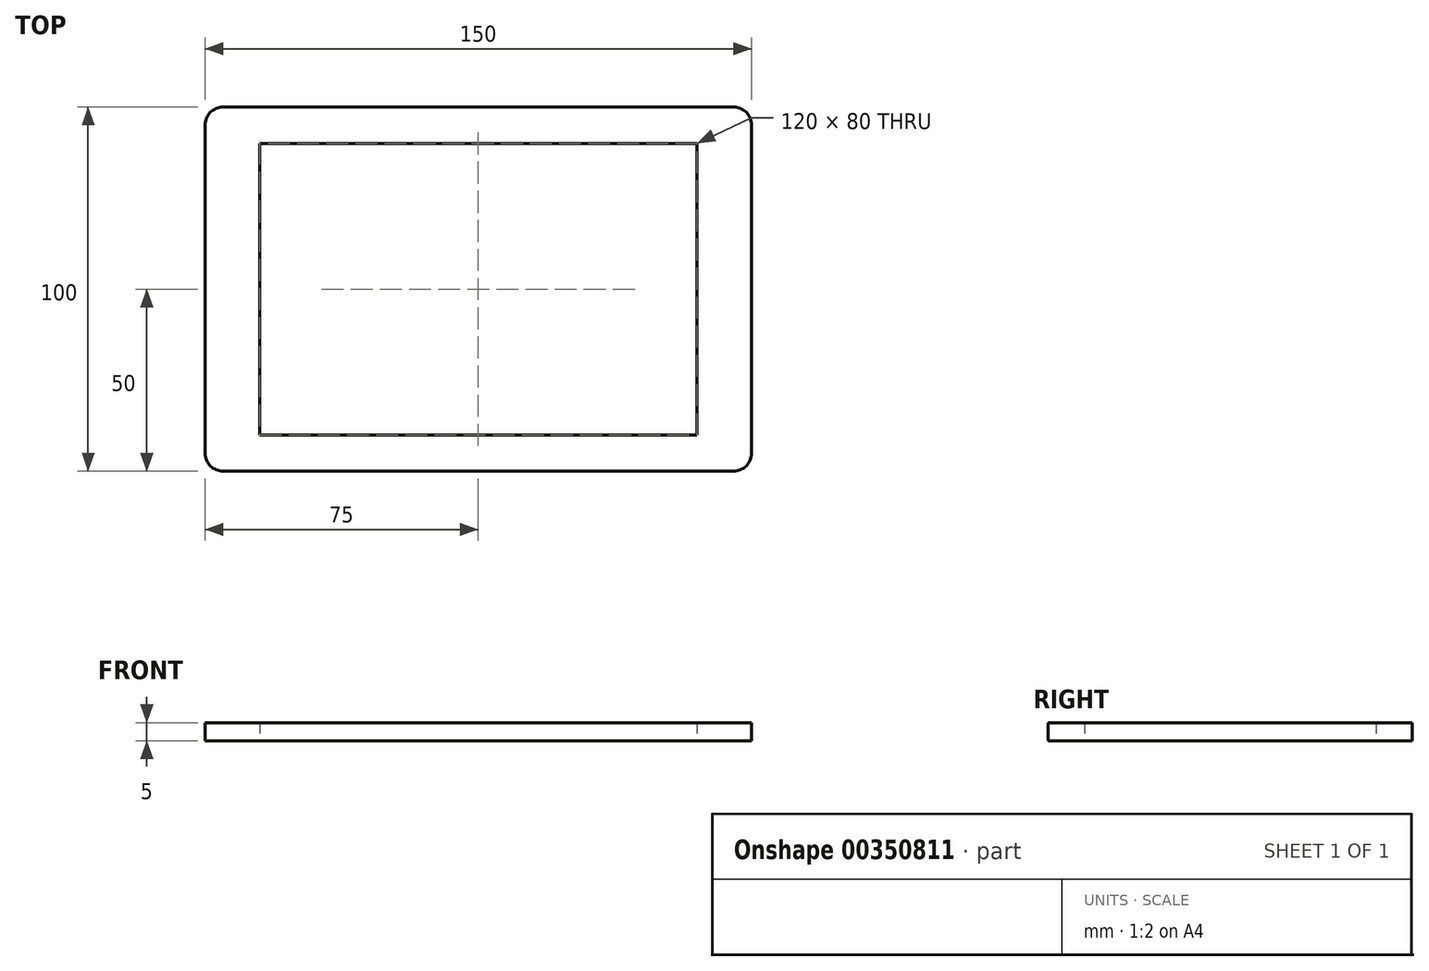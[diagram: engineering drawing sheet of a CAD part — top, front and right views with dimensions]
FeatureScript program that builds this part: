
annotation { "Feature Type Name" : "Feature", "Feature Type Description" : "" }
export const myFeature = defineFeature(function(context is Context, id is Id, definition is map)
    precondition{}
    {
        {
            var Q0;
            Q0=qCreatedBy(makeId("Top.planeOp"),FACE);
            var sketch = newSketch(context, id + "F0", { "sketchPlane" : qUnion([Q0])});
            skLineSegment(sketch, "E0.bottom", {"start": v(70, 50) * mm, "end": v(-70, 50) * mm});
            skLineSegment(sketch, "E0.top", {"start": v(70, -50) * mm, "end": v(-70, -50) * mm});
            skLineSegment(sketch, "E0.left", {"start": v(75, 45) * mm, "end": v(75, -45) * mm});
            skLineSegment(sketch, "E0.right", {"start": v(-75, 45) * mm, "end": v(-75, -45) * mm});
            skPoint(sketch, "E0.middle", {"position": v(0, 0) * mm});
            skPoint(sketch, "E1.visualSharp", {"position": v(-75, 50) * mm});
            skArc(sketch, "E1.filletArc", {"start": v(-70, 50) * mm, "mid": v(-73.54, 48.54) * mm, "end": v(-75, 45) * mm});
            skPoint(sketch, "E2.visualSharp", {"position": v(75, 50) * mm});
            skArc(sketch, "E2.filletArc", {"start": v(75, 45) * mm, "mid": v(73.54, 48.54) * mm, "end": v(70, 50) * mm});
            skPoint(sketch, "E3.visualSharp", {"position": v(75, -50) * mm});
            skArc(sketch, "E3.filletArc", {"start": v(70, -50) * mm, "mid": v(73.54, -48.54) * mm, "end": v(75, -45) * mm});
            skPoint(sketch, "E4.visualSharp", {"position": v(-75, -50) * mm});
            skArc(sketch, "E4.filletArc", {"start": v(-75, -45) * mm, "mid": v(-73.54, -48.54) * mm, "end": v(-70, -50) * mm});
            skLineSegment(sketch, "E5.bottom", {"start": v(60, -40) * mm, "end": v(-60, -40) * mm});
            skLineSegment(sketch, "E5.top", {"start": v(60, 40) * mm, "end": v(-60, 40) * mm});
            skLineSegment(sketch, "E5.left", {"start": v(60, -40) * mm, "end": v(60, 40) * mm});
            skLineSegment(sketch, "E5.right", {"start": v(-60, -40) * mm, "end": v(-60, 40) * mm});
            skSolve(sketch);
        }
        {
            var Q0;
            Q0 = qSketchRegion(id + "F0", true);
            extrude(context, id + "F1", {"entities" : qUnion([Q0]), "depth" : 5 * mm});
        }
    });
